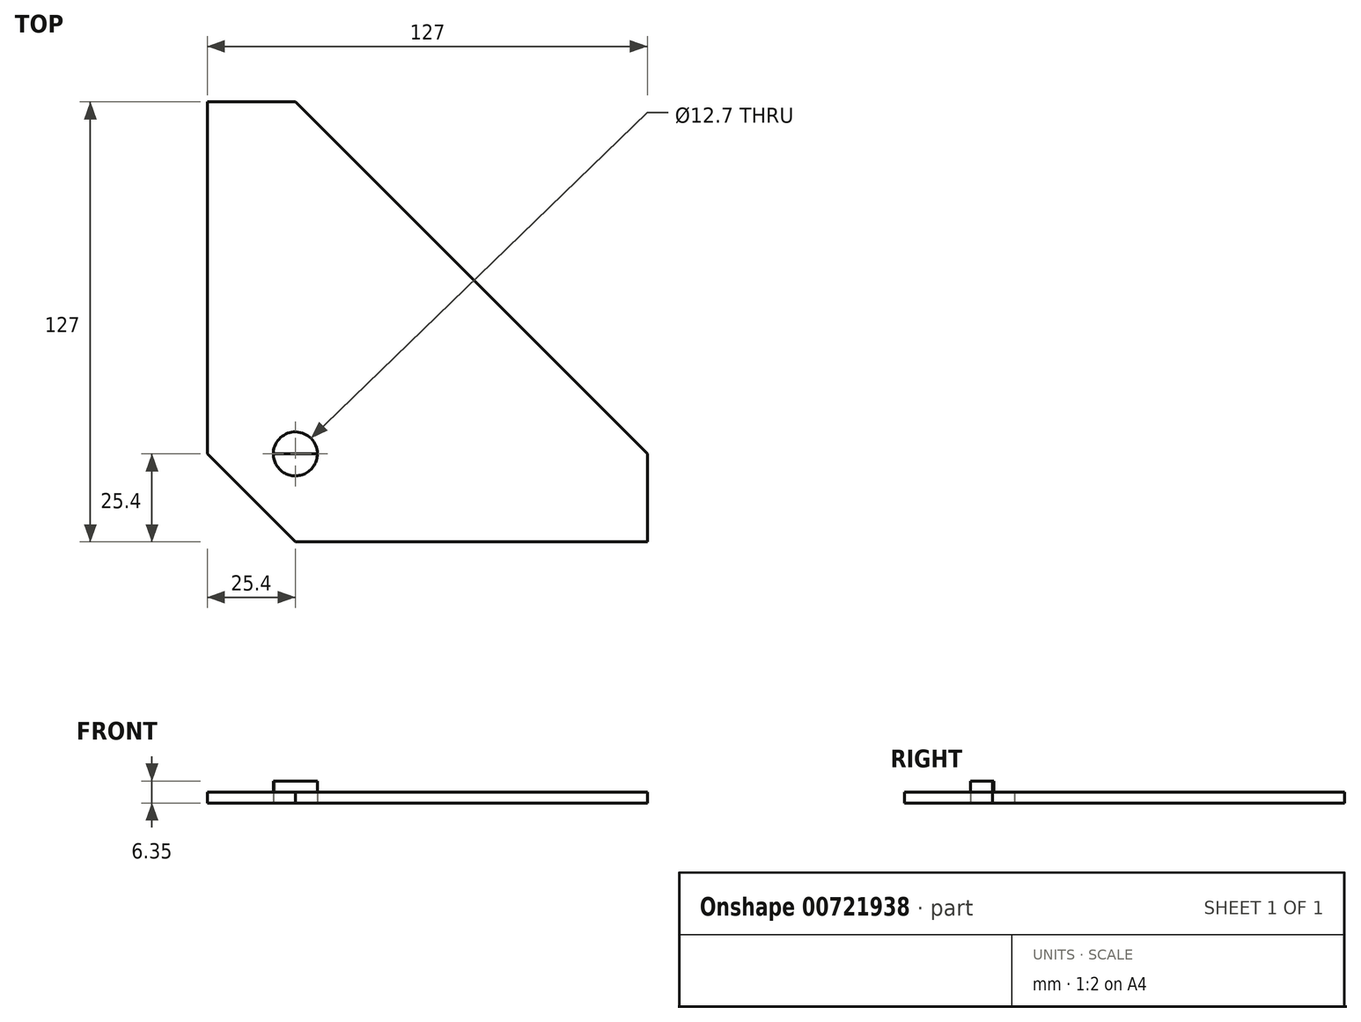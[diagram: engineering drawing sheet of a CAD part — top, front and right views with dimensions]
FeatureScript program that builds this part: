
annotation { "Feature Type Name" : "Feature", "Feature Type Description" : "" }
export const myFeature = defineFeature(function(context is Context, id is Id, definition is map)
    precondition{}
    {
        {
            var Q0;
            Q0=qCreatedBy(makeId("Top.planeOp"),FACE);
            var sketch = newSketch(context, id + "F0", { "sketchPlane" : qUnion([Q0])});
            skCircle(sketch, "E0", {"center": v(0, 0) * mm, "radius": 6.35 * mm});
            skLineSegment(sketch, "E1", {"start": v(-25.4, 0) * mm, "end": v(-25.4, 101.6) * mm});
            skLineSegment(sketch, "E2", {"start": v(-25.4, 101.6) * mm, "end": v(0, 101.6) * mm});
            skLineSegment(sketch, "E3", {"start": v(0, 101.6) * mm, "end": v(101.6, 0) * mm});
            skLineSegment(sketch, "E4", {"start": v(101.6, 0) * mm, "end": v(101.6, -25.4) * mm});
            skLineSegment(sketch, "E5", {"start": v(101.6, -25.4) * mm, "end": v(0, -25.4) * mm});
            skLineSegment(sketch, "E6", {"start": v(0, -25.4) * mm, "end": v(-25.4, 0) * mm});
            skLineSegment(sketch, "E7.left", {"start": v(101.6, -25.4) * mm, "end": v(101.6, -12.7) * mm});
            skSolve(sketch);
        }
        {
            var Q0;
            Q0 = qSketchRegion(id + "F0", true);
            extrude(context, id + "F1", {"entities" : qUnion([Q0]), "depth" : 3.17 * mm, "offsetDistance" : 25.4 * mm});
        }
        {
            var Q0;
            Q0=makeQuery(id+"F1.opExtrude","CAP_FACE",FACE,{"disambiguationData":[OSD([sQuery(id+"F0.wireOp",EDGE,"E0"),sQuery(id+"F0.wireOp",EDGE,"E1"),sQuery(id+"F0.wireOp",EDGE,"E2"),sQuery(id+"F0.wireOp",EDGE,"E3"),sQuery(id+"F0.wireOp",EDGE,"E4"),sQuery(id+"F0.wireOp",EDGE,"E5"),sQuery(id+"F0.wireOp",EDGE,"E6")])],"isStart":false});
            var sketch = newSketch(context, id + "F2", { "sketchPlane" : qUnion([Q0])});
            skLineSegment(sketch, "E8", {"start": v(101.6, 0) * mm, "end": v(-5.96, 0) * mm});
            skCircle(sketch, "E9", {"center": v(0, 0) * mm, "radius": 6.35 * mm});
            skCircle(sketch, "E10", {"center": v(0, 0) * mm, "radius": 7.94 * mm});
            skLineSegment(sketch, "E11", {"start": v(-12.7, 6.74) * mm, "end": v(-5.96, 0) * mm});
            skLineSegment(sketch, "E12", {"start": v(101.6, 0) * mm, "end": v(101.6, -25.4) * mm});
            skLineSegment(sketch, "E13", {"start": v(-12.7, 6.74) * mm, "end": v(-12.7, 101.6) * mm});
            skSolve(sketch);
        }
        {
            var Q0;
            Q0=makeQuery(id+"F2.imprint","IMPRINT",FACE,{"disambiguationData":[TD([[makeQuery(id+"F2.imprint","IMPRINT",EDGE,{"derivedFrom":sQuery(id+"F2.wireOp",EDGE,"E8")}),1.0]])]});
            extrude(context, id + "F3", {"entities" : qUnion([Q0]), "operationType" : NewBodyOperationType.ADD, "depth" : 3.17 * mm, "offsetDistance" : 25.4 * mm});
        }
    });
